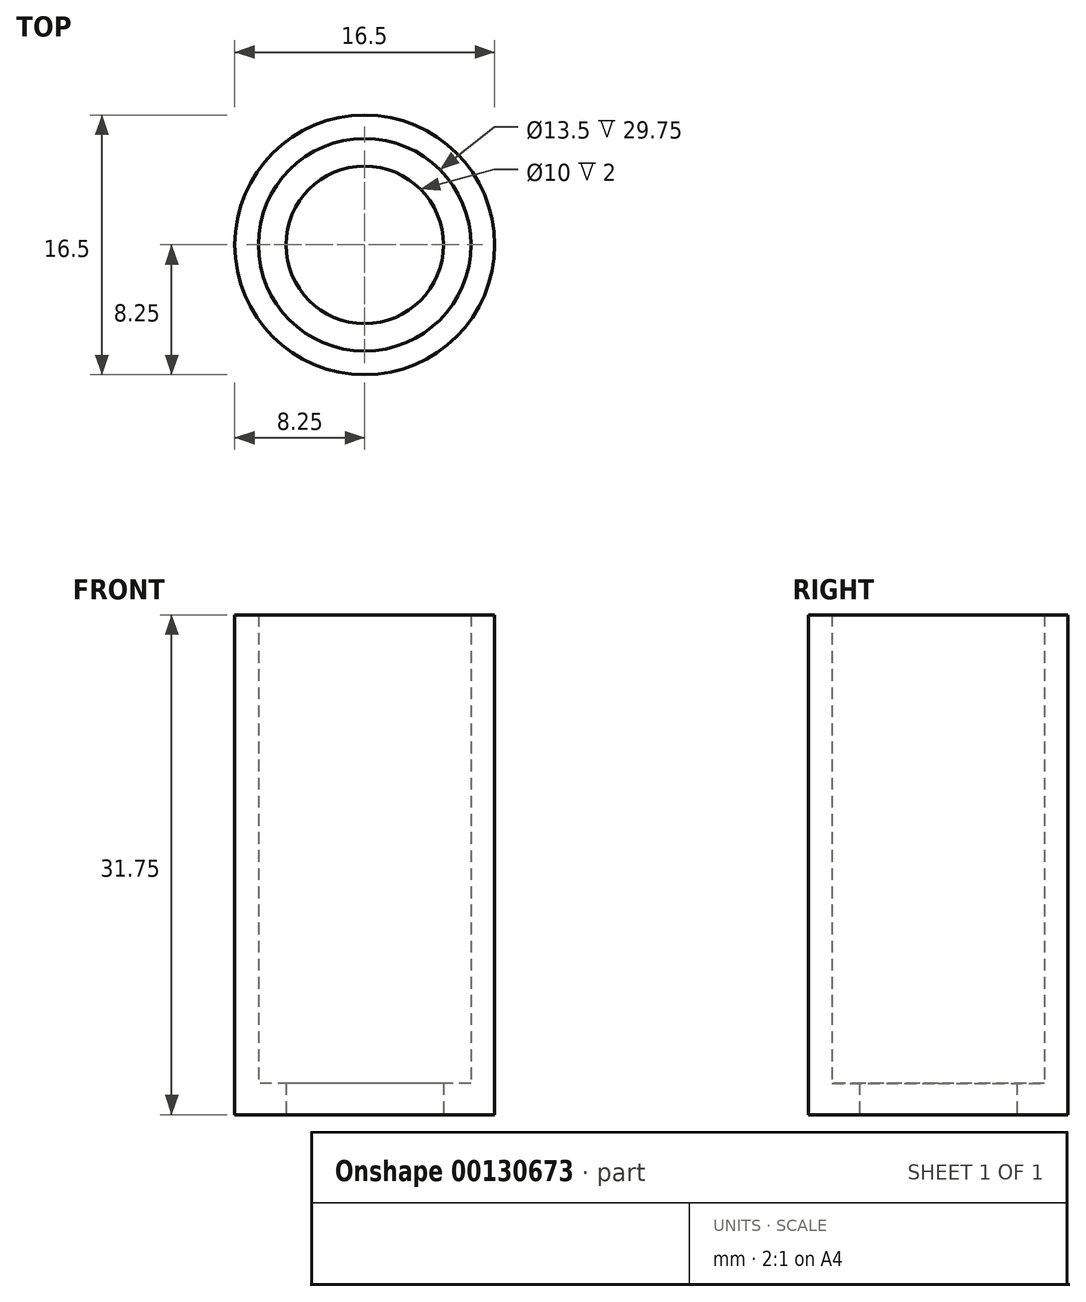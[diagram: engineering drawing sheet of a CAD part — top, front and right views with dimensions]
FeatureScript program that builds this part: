
annotation { "Feature Type Name" : "Feature", "Feature Type Description" : "" }
export const myFeature = defineFeature(function(context is Context, id is Id, definition is map)
    precondition{}
    {
        {
            var Q0;
            Q0=qCreatedBy(makeId("Top.planeOp"),FACE);
            var sketch = newSketch(context, id + "F0", { "sketchPlane" : qUnion([Q0])});
            skCircle(sketch, "E0", {"center": v(0, 0) * mm, "radius": 6.75 * mm});
            skCircle(sketch, "E1", {"center": v(0, 0) * mm, "radius": 8.25 * mm});
            skSolve(sketch);
        }
        {
            var Q0;
            Q0=makeQuery(id+"F0.imprint","IMPRINT",FACE,{"disambiguationData":[TD([[makeQuery(id+"F0.imprint","IMPRINT",EDGE,{"derivedFrom":sQuery(id+"F0.wireOp",EDGE,"E0")}),-1.0]])]});
            extrude(context, id + "F1", {"entities" : qUnion([Q0]), "depth" : 31.75 * mm});
        }
        {
            var Q0;
            Q0=qCreatedBy(makeId("Top.planeOp"),FACE);
            var sketch = newSketch(context, id + "F2", { "sketchPlane" : qUnion([Q0])});
            skCircle(sketch, "E2", {"center": v(0, 0) * mm, "radius": 8.08 * mm});
            skSolve(sketch);
        }
        {
            var Q0;
            Q0 = qSketchRegion(id + "F2", true);
            extrude(context, id + "F3", {"entities" : qUnion([Q0]), "operationType" : NewBodyOperationType.ADD, "depth" : 2 * mm});
        }
        {
            var Q0;
            Q0=makeQuery(id+"F3.boolean.opBoolean","MERGE",FACE,{"derivedFrom":[makeQuery(id+"F1.opExtrude","CAP_FACE",FACE,{"disambiguationData":[OSD([sQuery(id+"F0.wireOp",EDGE,"E0"),sQuery(id+"F0.wireOp",EDGE,"E1")])],"isStart":true}),makeQuery(id+"F3.opExtrude","CAP_FACE",FACE,{"disambiguationData":[OSD([sQuery(id+"F2.wireOp",EDGE,"E2")])],"isStart":true})]});
            var sketch = newSketch(context, id + "F4", { "sketchPlane" : qUnion([Q0])});
            skCircle(sketch, "E3", {"center": v(0, 0) * mm, "radius": 5 * mm});
            skSolve(sketch);
        }
        {
            var Q0;
            Q0 = qSketchRegion(id + "F4", true);
            extrude(context, id + "F5", {"entities" : qUnion([Q0]), "operationType" : NewBodyOperationType.REMOVE, "oppositeDirection" : true, "depth" : 25 * mm});
        }
    });
